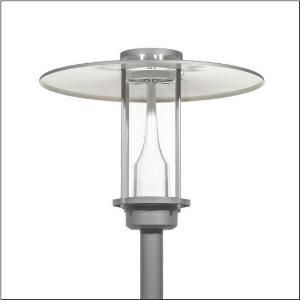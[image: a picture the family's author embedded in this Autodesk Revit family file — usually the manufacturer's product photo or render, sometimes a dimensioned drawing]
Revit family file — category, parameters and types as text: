
# Revit family: city-light_plus_iq___p1_0a_5xa5275lf14hp_bc32
name_source: partatom
category: Lighting Fixtures
units: mm (PartAtom-declared; Revit-internal decimal feet)

## family parameters
Cut with Voids When Loaded = No
Host = Face
Light Source = No
Part Type = Normal
Room Calculation Point = No
Round Connector Dimension = Use Diameter
Shared = No

## types (1)
- --- (1 x LED, 4680 lm, 33.6 W, 4000K)
    Apparent Load = 34 VA
    CIE Flux Codes = 30 60 90 96 100
    Color Rendering = 70
    Color Temperature = 4000K
    Default Elevation = 1800 mm
    Description = City-Light Plus iQ, mast luminaire, Module 540 iQ-SR, primary light control with 3 zone facetted reflector, of plastic, silver coated, highly specular, structured, primary optical cover: cover, of PMMA, transparent, light distribution: P1.0a, light emission: direct distribution, primary light characteristic: strongly asymmetric, installation type: post-top, LED, High Power LED, rated luminous flux: 4.680lm, luminous efficacy: 139lm/W, light colour: 740, colour temperature: 4000K, control gear: ECG iQ, control: pre-setting: logarithmic dimming characteristic, Street-Remote, Auto-Match, Temp-Guard, Lumen-Switch, Night-Set, Smart-Wire, Light-Fading, Desk-Remote (wireless, voltage-free reading and setting of iQ features in the workshop via application-optimized NFC function/RFID function), optimised constant luminous flux control (CLO 2.0), with terminal, 6-pole, max. 2.5mm², mains connection: 230..240V, AC, 50/60Hz, start of lifetime: 34W, end of service life: 36W, reduction: 15W, luminaire housing, upper part, of glass-fibre reinforced polyester, coated, Siteco® metallic grey (DB 702S), diameter: 750mm, height: 590mm, spigot size: d x l = 76 x 70mm (post-top) | with reducer (optional accessory) 60 x 70mm, post-top mast mounting element, of diecast aluminium, coated, Siteco® metallic grey (DB 702S), Module 540 iQ-SR, traffic white (RAL 9016), equipment: Power, protection rating (complete): IP65, insulation class (complete): insulation class II (safety insulation), certification: CE, ENEC, VDE, packaging unit: 1 piece

Light Distribution: P1.0a
    Height = 590 mm
    Lamp = 1 x LED
    Lamp Light Flux = 4680 lm
    Lamp Power = 33.6 W
    Lamp count = 1
    Length = 750 mm
    Luminous efficacy = 139 lm/W
    Manufacturer = Siteco
    ModVariant = No
    Model = 5XA5275LF14HP
    Number of Poles = 1
    OnlyDefault = Yes
    Power Factor = 1
    Product Name = City-Light Plus iQ | P1.0a
    Product group = mast luminaire | pylon top
    ProductGroupID = 6100
    Protection Class = Protection class II
    Protection Degree = IP 65
    RLX_Detail_Level = 1
    RLX_Emergency_Light_Flux = 0 lm
    RLX_Emergency_Type = 0
    RLX_Emergency_Type_DB = No
    RlxData = <blob elided: 52589 chars, md5=75f029d2>
    Socket = socket
    Standby Power = 0 W
    System Light Flux = 4680 lm
    System Power = 34 W
    Type Comments = factory setting: luminous flux: 100 % | dim-lin: 254 | 695 mA
    Type Image = l_1006456.jpg
    URL = http://relux.com
    VarID = @adj_166381
    Voltage = 0 V
    Weight = 0.00 kg
    Width = 0 mm  [stored 0 ft]

note: [stored X ft] marks values corroborated as IEEE doubles in the binary element streams (Revit-internal decimal feet)

## geometry (parser evidence)
native form markers: Blend x4, Sweep x11
no freeform markers — native parametric forms only
